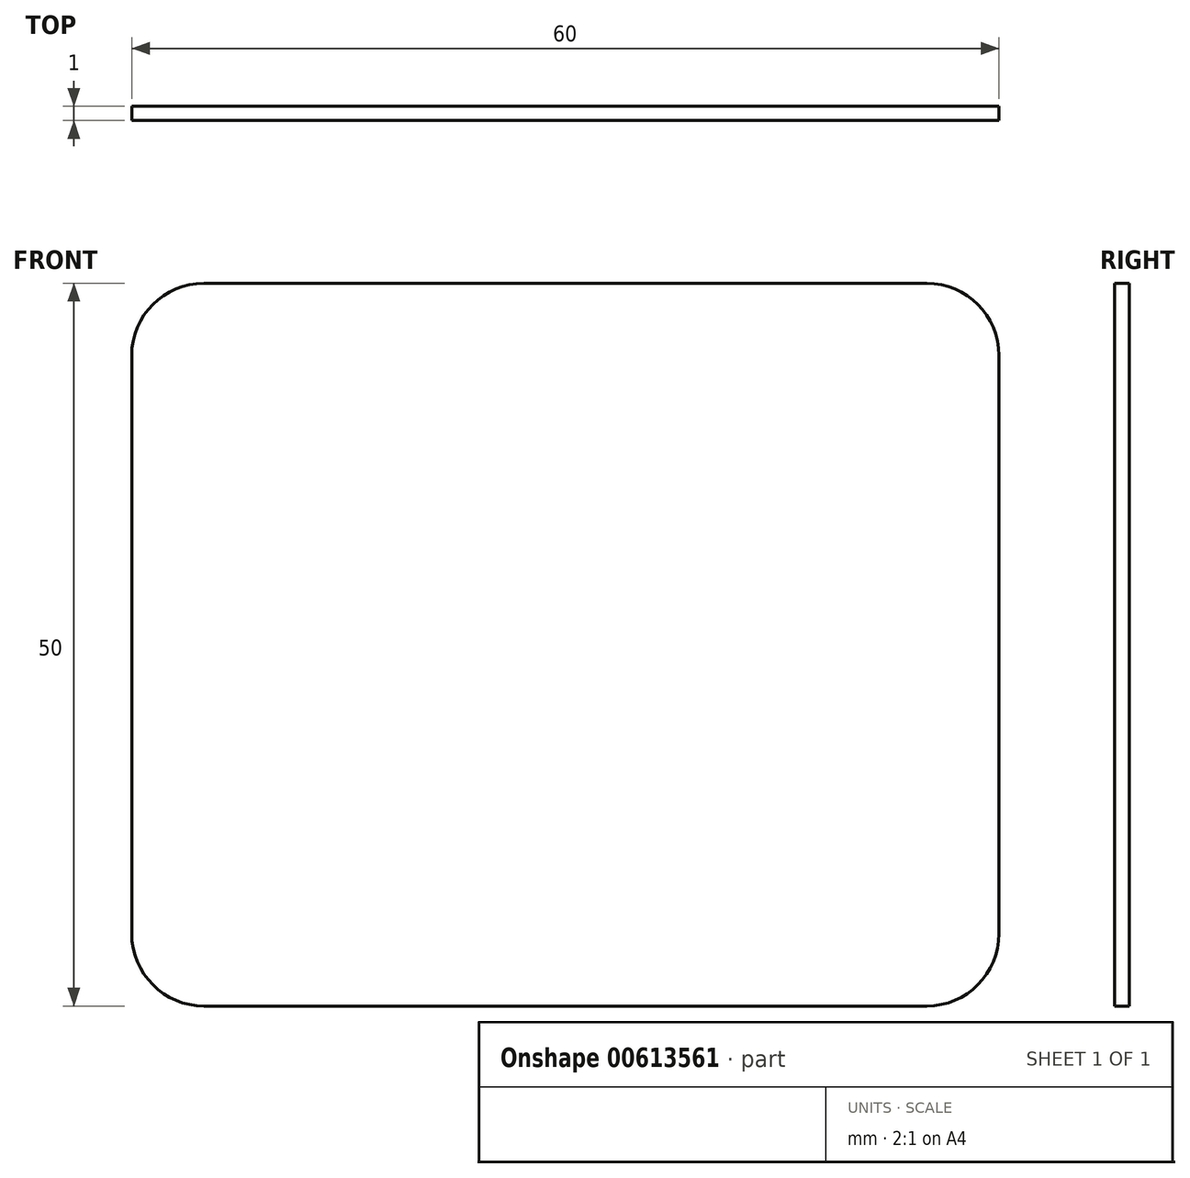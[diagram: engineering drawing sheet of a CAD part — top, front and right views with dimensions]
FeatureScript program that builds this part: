
annotation { "Feature Type Name" : "Feature", "Feature Type Description" : "" }
export const myFeature = defineFeature(function(context is Context, id is Id, definition is map)
    precondition{}
    {
        {
            var Q0;
            Q0=qCreatedBy(makeId("Front.planeOp"),FACE);
            var sketch = newSketch(context, id + "F0", { "sketchPlane" : qUnion([Q0])});
            skLineSegment(sketch, "E0.bottom", {"start": v(-5, 0) * mm, "end": v(-55, 0) * mm});
            skLineSegment(sketch, "E0.top", {"start": v(-5, 50) * mm, "end": v(-55, 50) * mm});
            skLineSegment(sketch, "E0.left", {"start": v(0, 5) * mm, "end": v(0, 45) * mm});
            skLineSegment(sketch, "E0.right", {"start": v(-60, 5) * mm, "end": v(-60, 45) * mm});
            skPoint(sketch, "E1.visualSharp", {"position": v(-60, 50) * mm});
            skArc(sketch, "E1.filletArc", {"start": v(-55, 50) * mm, "mid": v(-58.54, 48.54) * mm, "end": v(-60, 45) * mm});
            skPoint(sketch, "E2.visualSharp", {"position": v(0, 50) * mm});
            skArc(sketch, "E2.filletArc", {"start": v(0, 45) * mm, "mid": v(-1.46, 48.54) * mm, "end": v(-5, 50) * mm});
            skPoint(sketch, "E3.visualSharp", {"position": v(0, 0) * mm});
            skArc(sketch, "E3.filletArc", {"start": v(-5, 0) * mm, "mid": v(-1.46, 1.46) * mm, "end": v(0, 5) * mm});
            skPoint(sketch, "E4.visualSharp", {"position": v(-60, 0) * mm});
            skArc(sketch, "E4.filletArc", {"start": v(-60, 5) * mm, "mid": v(-58.54, 1.46) * mm, "end": v(-55, 0) * mm});
            skSolve(sketch);
        }
        {
            var Q0;
            Q0 = qSketchRegion(id + "F0", true);
            extrude(context, id + "F1", {"entities" : qUnion([Q0]), "depth" : 1 * mm, "offsetDistance" : 25 * mm});
        }
    });
